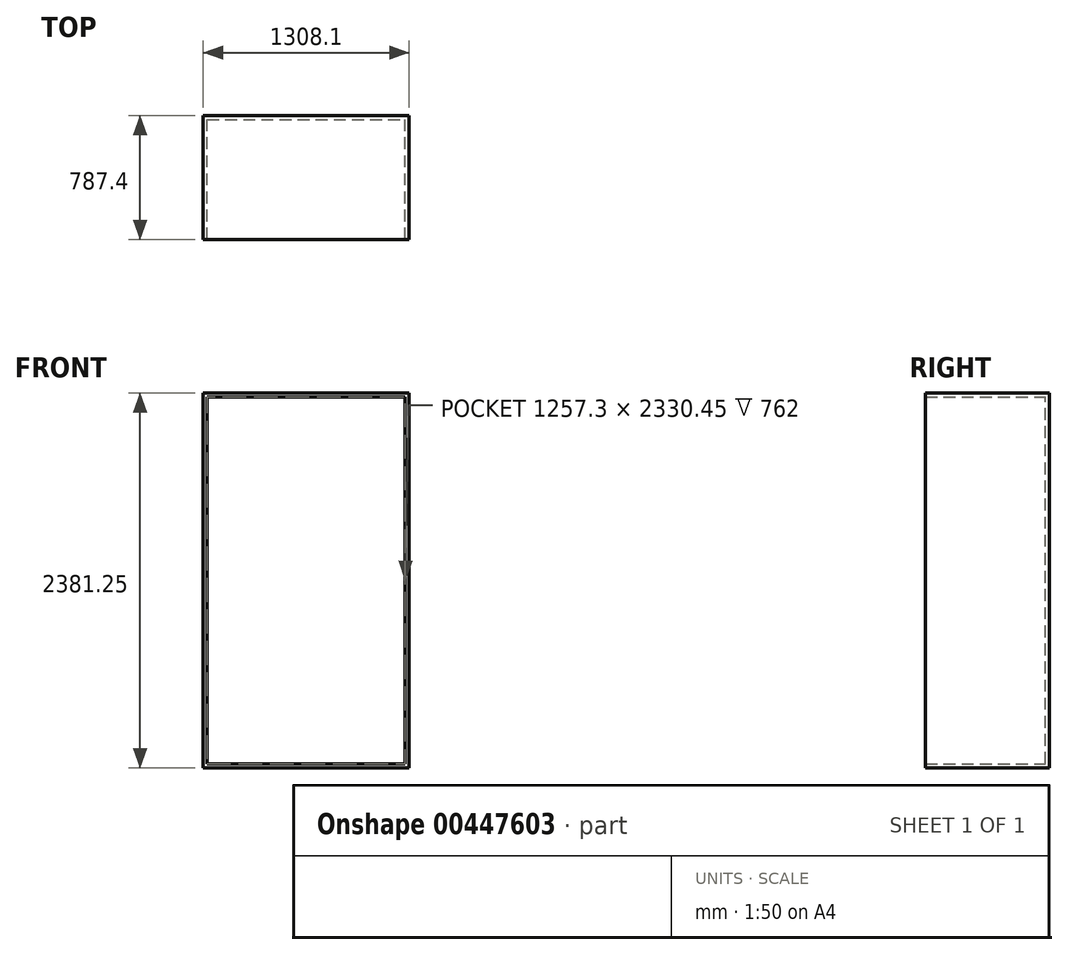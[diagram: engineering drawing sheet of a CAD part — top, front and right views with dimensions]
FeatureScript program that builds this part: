
annotation { "Feature Type Name" : "Feature", "Feature Type Description" : "" }
export const myFeature = defineFeature(function(context is Context, id is Id, definition is map)
    precondition{}
    {
        {
            var Q0;
            Q0=qCreatedBy(makeId("Front.planeOp"),FACE);
            var sketch = newSketch(context, id + "F0", { "sketchPlane" : qUnion([Q0])});
            skLineSegment(sketch, "E0.bottom", {"start": v(0, 0) * mm, "end": v(1308.1, 0) * mm});
            skLineSegment(sketch, "E0.top", {"start": v(0, 2381.25) * mm, "end": v(1308.1, 2381.25) * mm});
            skLineSegment(sketch, "E0.left", {"start": v(0, 0) * mm, "end": v(0, 2381.25) * mm});
            skLineSegment(sketch, "E0.right", {"start": v(1308.1, 0) * mm, "end": v(1308.1, 2381.25) * mm});
            skSolve(sketch);
        }
        {
            var Q0;
            Q0 = qSketchRegion(id + "F0", true);
            extrude(context, id + "F1", {"entities" : qUnion([Q0]), "depth" : 787.4 * mm, "offsetDistance" : 25.4 * mm});
        }
        {
            var Q0;
            Q0=makeQuery(id+"F1.opExtrude","CAP_FACE",FACE,{"disambiguationData":[OSD([sQuery(id+"F0.wireOp",EDGE,"E0.bottom"),sQuery(id+"F0.wireOp",EDGE,"E0.top"),sQuery(id+"F0.wireOp",EDGE,"E0.left"),sQuery(id+"F0.wireOp",EDGE,"E0.right")])],"isStart":false});
            shell(context, id + "F2", {"entities" : qUnion([Q0]), "thickness" : 25.4 * mm});
        }
    });
